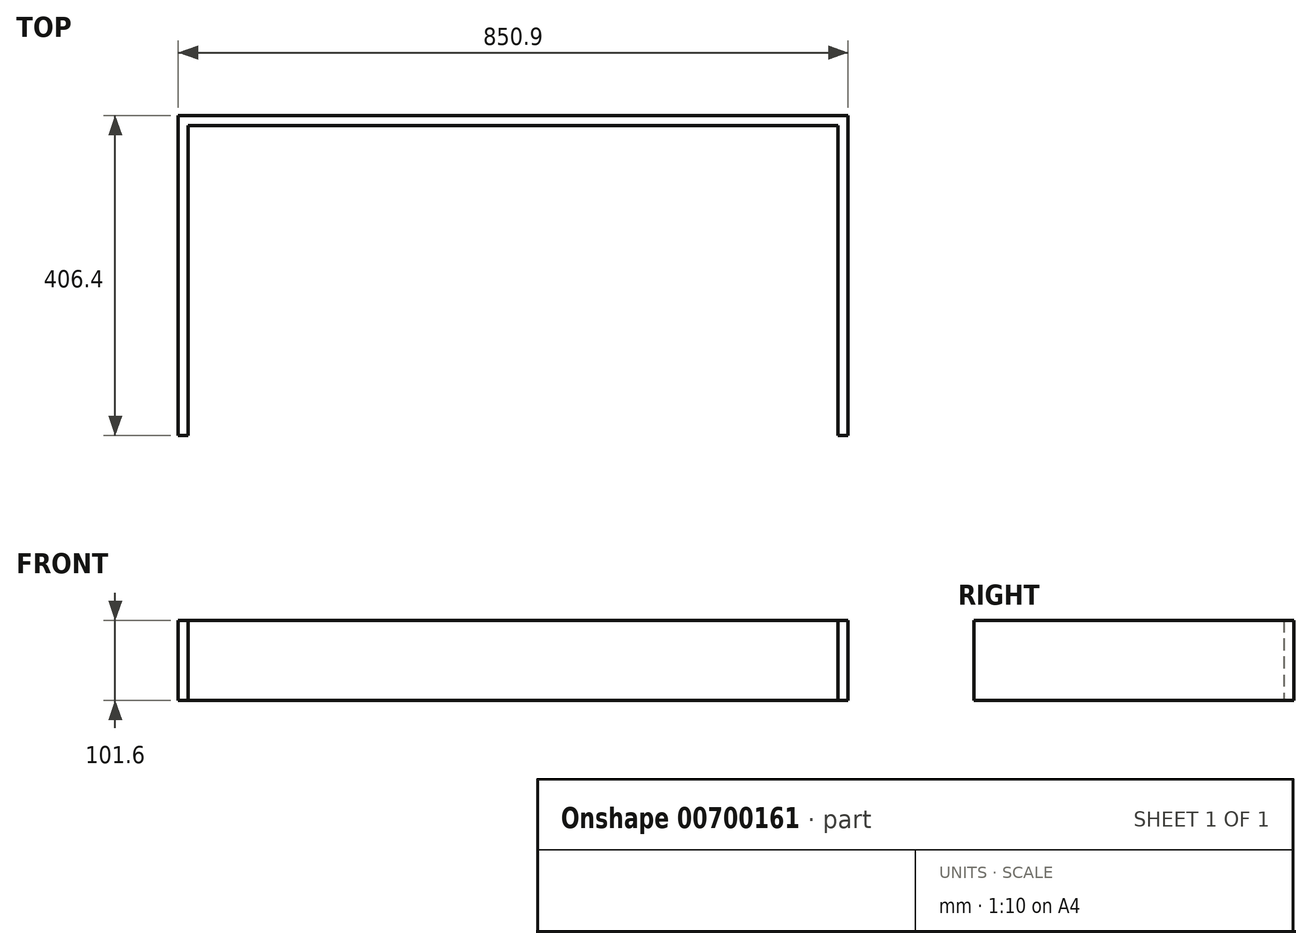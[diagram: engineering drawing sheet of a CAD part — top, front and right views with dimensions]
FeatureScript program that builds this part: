
annotation { "Feature Type Name" : "Feature", "Feature Type Description" : "" }
export const myFeature = defineFeature(function(context is Context, id is Id, definition is map)
    precondition{}
    {
        {
            var Q0;
            Q0=qCreatedBy(makeId("Top.planeOp"),FACE);
            var sketch = newSketch(context, id + "F0", { "sketchPlane" : qUnion([Q0])});
            skLineSegment(sketch, "E0.bottom", {"start": v(425.45, 203.2) * mm, "end": v(-425.45, 203.2) * mm});
            skLineSegment(sketch, "E0.top", {"start": v(425.45, -203.2) * mm, "end": v(-425.45, -203.2) * mm});
            skLineSegment(sketch, "E0.left", {"start": v(425.45, 203.2) * mm, "end": v(425.45, -203.2) * mm});
            skLineSegment(sketch, "E0.right", {"start": v(-425.45, 203.2) * mm, "end": v(-425.45, -203.2) * mm});
            skPoint(sketch, "E0.middle", {"position": v(0, 0) * mm});
            skLineSegment(sketch, "E1.bottom", {"start": v(-412.75, 190.5) * mm, "end": v(412.75, 190.5) * mm});
            skLineSegment(sketch, "E1.top", {"start": v(-412.75, -190.5) * mm, "end": v(412.75, -190.5) * mm});
            skLineSegment(sketch, "E1.left", {"start": v(-412.75, 190.5) * mm, "end": v(-412.75, -190.5) * mm});
            skLineSegment(sketch, "E1.right", {"start": v(412.75, 190.5) * mm, "end": v(412.75, -190.5) * mm});
            skLineSegment(sketch, "E2", {"start": v(-412.75, -190.5) * mm, "end": v(-412.75, -203.2) * mm});
            skLineSegment(sketch, "E3", {"start": v(412.75, -190.5) * mm, "end": v(412.75, -203.2) * mm});
            skSolve(sketch);
        }
        {
            var Q0;
            Q0=makeQuery(id+"F0.imprint","IMPRINT",FACE,{"disambiguationData":[TD([[makeQuery(id+"F0.imprint","IMPRINT",EDGE,{"derivedFrom":sQuery(id+"F0.wireOp",EDGE,"E0.bottom")}),1.0]])]});
            extrude(context, id + "F1", {"entities" : qUnion([Q0]), "depth" : 101.6 * mm, "offsetDistance" : 25.4 * mm});
        }
    });
